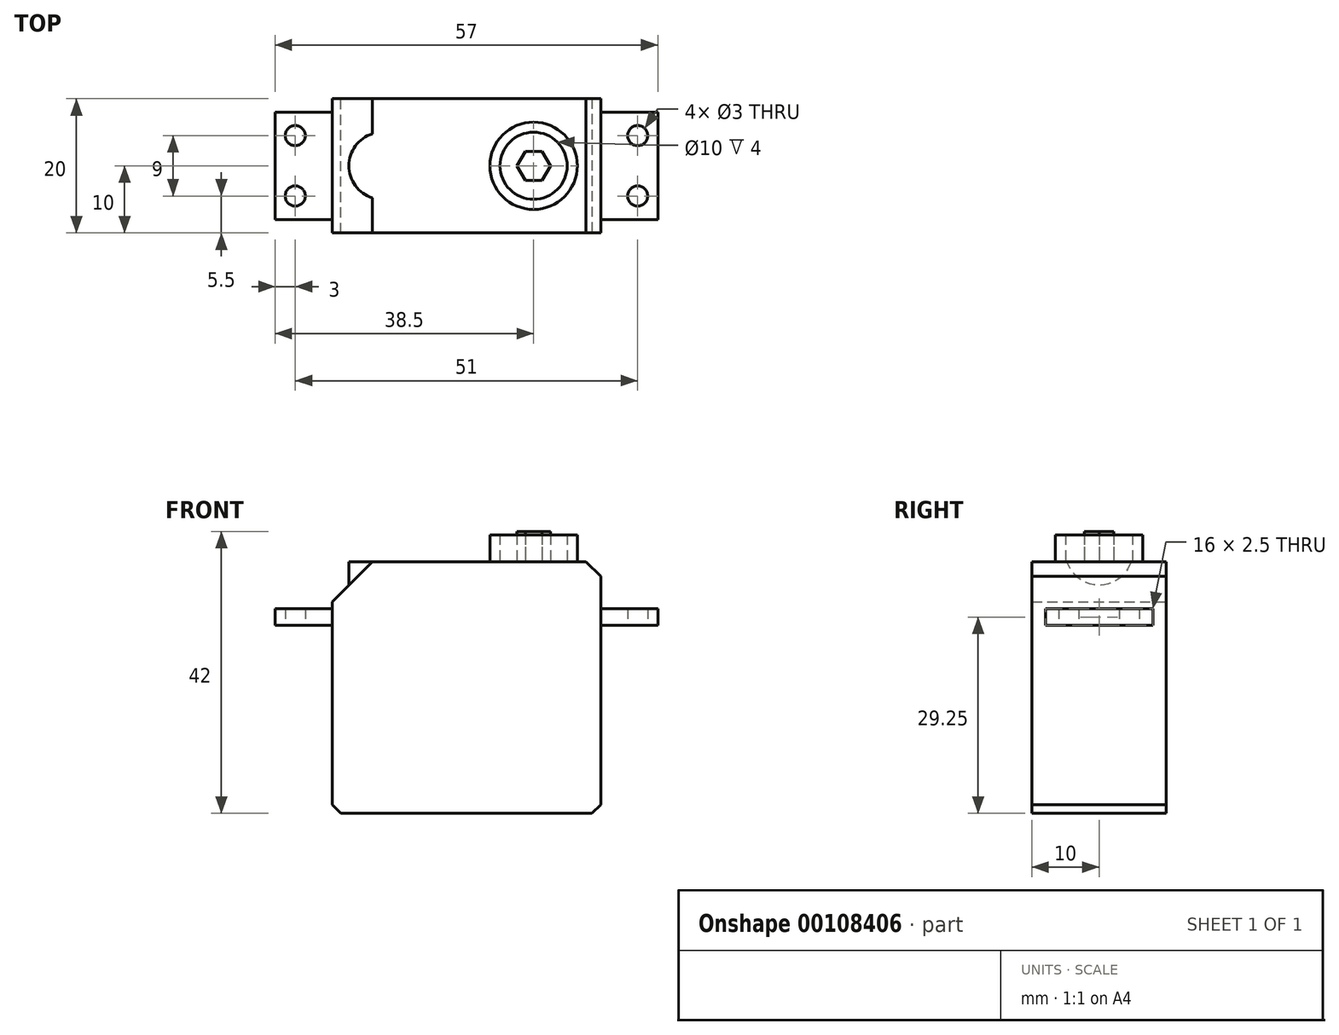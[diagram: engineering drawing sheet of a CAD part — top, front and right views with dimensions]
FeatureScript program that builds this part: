
annotation { "Feature Type Name" : "Feature", "Feature Type Description" : "" }
export const myFeature = defineFeature(function(context is Context, id is Id, definition is map)
    precondition{}
    {
        {
            var Q0;
            Q0=qCreatedBy(makeId("Top.planeOp"),FACE);
            var sketch = newSketch(context, id + "F0", { "sketchPlane" : qUnion([Q0])});
            skLineSegment(sketch, "E0.bottom", {"start": v(-20, 10) * mm, "end": v(20, 10) * mm});
            skLineSegment(sketch, "E0.top", {"start": v(-20, -10) * mm, "end": v(20, -10) * mm});
            skLineSegment(sketch, "E0.left", {"start": v(-20, 10) * mm, "end": v(-20, -10) * mm});
            skLineSegment(sketch, "E0.right", {"start": v(20, 10) * mm, "end": v(20, -10) * mm});
            skPoint(sketch, "E0.middle", {"position": v(0, 0) * mm});
            skLineSegment(sketch, "E1", {"start": v(-20, 0) * mm, "end": v(10, 0) * mm, "construction": true});
            skLineSegment(sketch, "E2", {"start": v(20, 10) * mm, "end": v(20, 8) * mm});
            skLineSegment(sketch, "E3", {"start": v(20, -10) * mm, "end": v(20, -8) * mm});
            skLineSegment(sketch, "E4", {"start": v(-20, -10) * mm, "end": v(-20, -8) * mm});
            skLineSegment(sketch, "E5", {"start": v(-20, 10) * mm, "end": v(-20, 8) * mm});
            skLineSegment(sketch, "E6", {"start": v(20, 8) * mm, "end": v(28.5, 8) * mm});
            skLineSegment(sketch, "E7", {"start": v(20, -8) * mm, "end": v(28.5, -8) * mm});
            skLineSegment(sketch, "E8", {"start": v(-20, -8) * mm, "end": v(-28.5, -8) * mm});
            skLineSegment(sketch, "E9", {"start": v(-20, 8) * mm, "end": v(-28.5, 8) * mm});
            skLineSegment(sketch, "E10", {"start": v(28.5, -8) * mm, "end": v(28.5, 8) * mm});
            skLineSegment(sketch, "E11", {"start": v(-28.5, -8) * mm, "end": v(-28.5, 8) * mm});
            skCircle(sketch, "E12.cCircle", {"center": v(10, 0) * mm, "radius": 2.17 * mm, "construction": true});
            skLineSegment(sketch, "E12.0", {"start": v(8.75, 2.17) * mm, "end": v(11.25, 2.17) * mm});
            skLineSegment(sketch, "E12.1", {"start": v(11.25, 2.17) * mm, "end": v(12.5, 0) * mm});
            skLineSegment(sketch, "E12.2", {"start": v(12.5, 0) * mm, "end": v(11.25, -2.17) * mm});
            skLineSegment(sketch, "E12.3", {"start": v(11.25, -2.17) * mm, "end": v(8.75, -2.17) * mm});
            skLineSegment(sketch, "E12.4", {"start": v(8.75, -2.17) * mm, "end": v(7.5, 0) * mm});
            skLineSegment(sketch, "E12.5", {"start": v(7.5, 0) * mm, "end": v(8.75, 2.17) * mm});
            skPoint(sketch, "E12.0.midPoint", {"position": v(10, 2.17) * mm});
            skCircle(sketch, "E13", {"center": v(10, 0) * mm, "radius": 5 * mm});
            skLineSegment(sketch, "E14", {"start": v(-20, 0) * mm, "end": v(-5.25, 0) * mm, "construction": true});
            skPoint(sketch, "E15.middle", {"position": v(-5.25, 0) * mm});
            skLineSegment(sketch, "E16", {"start": v(-28.5, 0) * mm, "end": v(-25.5, 0) * mm, "construction": true});
            skPoint(sketch, "E16.endSnap0", {"position": v(-28.5, 0) * mm});
            skLineSegment(sketch, "E17", {"start": v(-25.5, 0) * mm, "end": v(-25.5, 4.5) * mm, "construction": true});
            skLineSegment(sketch, "E18", {"start": v(-25.5, 0) * mm, "end": v(-25.5, -4.5) * mm, "construction": true});
            skCircle(sketch, "E19", {"center": v(-25.5, 4.5) * mm, "radius": 1.5 * mm});
            skCircle(sketch, "E20", {"center": v(-25.5, -4.5) * mm, "radius": 1.5 * mm});
            skLineSegment(sketch, "E21", {"start": v(28.5, 0) * mm, "end": v(25.5, 0) * mm, "construction": true});
            skPoint(sketch, "E21.endSnap0", {"position": v(28.5, 0) * mm});
            skLineSegment(sketch, "E22", {"start": v(25.5, 0) * mm, "end": v(25.5, 4.5) * mm, "construction": true});
            skLineSegment(sketch, "E23", {"start": v(25.5, 0) * mm, "end": v(25.5, -4.5) * mm, "construction": true});
            skCircle(sketch, "E24", {"center": v(25.5, 4.5) * mm, "radius": 1.5 * mm});
            skCircle(sketch, "E25", {"center": v(25.5, -4.5) * mm, "radius": 1.5 * mm});
            skCircle(sketch, "E26", {"center": v(10, 0) * mm, "radius": 6.5 * mm});
            skLineSegment(sketch, "E27", {"start": v(20, 0) * mm, "end": v(19.5, 0) * mm});
            skCircle(sketch, "E28", {"center": v(10, 0) * mm, "radius": 9.5 * mm});
            skLineSegment(sketch, "E29", {"start": v(-20, 0) * mm, "end": v(-12.5, 0) * mm});
            skCircle(sketch, "E30", {"center": v(-12.5, 0) * mm, "radius": 5 * mm});
            skLineSegment(sketch, "E31", {"start": v(10, 0) * mm, "end": v(10, -6.5) * mm});
            skLineSegment(sketch, "E32", {"start": v(10, -6.5) * mm, "end": v(10, 6.5) * mm});
            skLineSegment(sketch, "E33", {"start": v(10, 0) * mm, "end": v(10, 5) * mm});
            skLineSegment(sketch, "E34", {"start": v(10, 0) * mm, "end": v(10, -5) * mm});
            skPoint(sketch, "E34.endSnap0", {"position": v(10, -3.25) * mm});
            skSolve(sketch);
        }
        {
            var Q0;
            Q0=makeQuery(id+"F0.imprint","IMPRINT",FACE,{"disambiguationData":[TD([[makeQuery(id+"F0.imprint","IMPRINT",EDGE,{"derivedFrom":sQuery(id+"F0.wireOp",EDGE,"E12.0")}),-1.0]])]});
            extrude(context, id + "F1", {"entities" : qUnion([Q0]), "depth" : 14 * mm});
        }
        {
            var Q0;
            Q0=makeQuery(id+"F0.imprint","IMPRINT",FACE,{"disambiguationData":[TD([[makeQuery(id+"F0.imprint","IMPRINT",EDGE,{"derivedFrom":sQuery(id+"F0.wireOp",EDGE,"E13")}),-1.0]])]});
            extrude(context, id + "F2", {"entities" : qUnion([Q0]), "operationType" : NewBodyOperationType.ADD, "depth" : 13.5 * mm});
        }
        {
            var Q0;
            Q0=makeQuery(id+"F0.imprint","IMPRINT",FACE,{"disambiguationData":[TD([[makeQuery(id+"F0.imprint","IMPRINT",EDGE,{"derivedFrom":sQuery(id+"F0.wireOp",EDGE,"E26")}),-1.0]])]});
            var Q1;
            Q1=makeQuery(id+"F0.imprint","IMPRINT",FACE,{"disambiguationData":[TD([[makeQuery(id+"F0.imprint","IMPRINT",EDGE,{"derivedFrom":sQuery(id+"F0.wireOp",EDGE,"E12.0")}),1.0]])]});
            extrude(context, id + "F3", {"entities" : qUnion([Q0, Q1]), "operationType" : NewBodyOperationType.ADD, "depth" : 9.5 * mm});
        }
        {
            var Q0;
            Q0=makeQuery(id+"F0.imprint","IMPRINT",FACE,{"disambiguationData":[TD([[makeQuery(id+"F0.imprint","IMPRINT",EDGE,{"derivedFrom":sQuery(id+"F0.wireOp",EDGE,"E0.bottom")}),-1.0]])]});
            var Q1;
            Q1=makeQuery(id+"F0.imprint","IMPRINT",FACE,{"disambiguationData":[TD([[makeQuery(id+"F0.imprint","IMPRINT",EDGE,{"derivedFrom":sQuery(id+"F0.wireOp",EDGE,"E26")}),-1.0]])]});
            extrude(context, id + "F4", {"entities" : qUnion([Q0, Q1]), "operationType" : NewBodyOperationType.ADD, "depth" : 9.5 * mm});
        }
        {
            var Q0;
            Q0=makeQuery(id+"F0.imprint","IMPRINT",FACE,{"disambiguationData":[TD([[makeQuery(id+"F0.imprint","IMPRINT",EDGE,{"derivedFrom":sQuery(id+"F0.wireOp",EDGE,"E0.bottom")}),-1.0]])]});
            var Q1;
            Q1=makeQuery(id+"F0.imprint","IMPRINT",FACE,{"disambiguationData":[TD([[makeQuery(id+"F0.imprint","IMPRINT",EDGE,{"derivedFrom":sQuery(id+"F0.wireOp",EDGE,"E26")}),-1.0]])]});
            var Q2;
            Q2=makeQuery(id+"F0.imprint","IMPRINT",FACE,{"disambiguationData":[TD([[makeQuery(id+"F0.imprint","IMPRINT",EDGE,{"derivedFrom":sQuery(id+"F0.wireOp",EDGE,"E12.0")}),-1.0]])]});
            var Q3;
            Q3=makeQuery(id+"F0.imprint","IMPRINT",FACE,{"disambiguationData":[TD([[makeQuery(id+"F0.imprint","IMPRINT",EDGE,{"derivedFrom":sQuery(id+"F0.wireOp",EDGE,"E12.0")}),1.0]])]});
            var Q4;
            Q4=makeQuery(id+"F0.imprint","IMPRINT",FACE,{"disambiguationData":[TD([[makeQuery(id+"F0.imprint","IMPRINT",EDGE,{"derivedFrom":sQuery(id+"F0.wireOp",EDGE,"E13")}),-1.0]])]});
            var Q5;
            Q5=makeQuery(id+"F0.imprint","IMPRINT",FACE,{"disambiguationData":[TD([[makeQuery(id+"F0.imprint","IMPRINT",EDGE,{"derivedFrom":sQuery(id+"F0.wireOp",EDGE,"E30")}),1.0]])]});
            extrude(context, id + "F5", {"entities" : qUnion([Q0, Q1, Q2, Q3, Q4, Q5]), "operationType" : NewBodyOperationType.ADD, "oppositeDirection" : true, "depth" : 28 * mm});
        }
        {
            var Q0;
            {var subQ1=sQuery(id+"F0.wireOp",EDGE,"E6");Q0=makeQuery(id+"F0.imprint","IMPRINT",FACE,{"disambiguationData":[TD([[makeQuery(id+"F0.imprint","IMPRINT",EDGE,{"derivedFrom":subQ1}),-1.0]])]});}
            var Q1;
            Q1=makeQuery(id+"F0.imprint","IMPRINT",FACE,{"disambiguationData":[TD([[makeQuery(id+"F0.imprint","IMPRINT",EDGE,{"derivedFrom":sQuery(id+"F0.wireOp",EDGE,"E0.left")}),-1.0]])]});
            extrude(context, id + "F6", {"entities" : qUnion([Q0, Q1]), "operationType" : NewBodyOperationType.ADD, "depth" : 2.5 * mm});
        }
        {
            var Q0;
            Q0=makeQuery(id+"F4.opExtrude","CAP_EDGE",EDGE,{"disambiguationData":[OSD([sQuery(id+"F0.wireOp",EDGE,"E0.right"),sQuery(id+"F0.wireOp",EDGE,"E2"),sQuery(id+"F0.wireOp",EDGE,"E3")])],"isStart":false});
            chamfer(context, id + "F7", {"entities" : qUnion([Q0]), "width" : 2.2 * mm});
        }
        {
            var Q0;
            Q0=makeQuery(id+"F4.opExtrude","CAP_EDGE",EDGE,{"disambiguationData":[OSD([sQuery(id+"F0.wireOp",EDGE,"E0.left"),sQuery(id+"F0.wireOp",EDGE,"E4"),sQuery(id+"F0.wireOp",EDGE,"E5")])],"isStart":false});
            chamfer(context, id + "F8", {"entities" : qUnion([Q0]), "width" : 6 * mm, "tangentPropagation" : true});
        }
        {
            var Q0;
            Q0=makeQuery(id+"F0.imprint","IMPRINT",FACE,{"disambiguationData":[TD([[makeQuery(id+"F0.imprint","IMPRINT",EDGE,{"derivedFrom":sQuery(id+"F0.wireOp",EDGE,"E30")}),1.0]])]});
            extrude(context, id + "F9", {"entities" : qUnion([Q0]), "operationType" : NewBodyOperationType.ADD, "depth" : 9.5 * mm});
        }
        {
            var Q0;
            Q0=makeQuery(id+"F5.opExtrude","CAP_EDGE",EDGE,{"disambiguationData":[OSD([sQuery(id+"F0.wireOp",EDGE,"E0.right"),sQuery(id+"F0.wireOp",EDGE,"E2"),sQuery(id+"F0.wireOp",EDGE,"E3")])],"isStart":false});
            var Q1;
            Q1=makeQuery(id+"F5.opExtrude","CAP_EDGE",EDGE,{"disambiguationData":[OSD([sQuery(id+"F0.wireOp",EDGE,"E0.left"),sQuery(id+"F0.wireOp",EDGE,"E4"),sQuery(id+"F0.wireOp",EDGE,"E5")])],"isStart":false});
            chamfer(context, id + "F10", {"entities" : qUnion([Q0, Q1]), "width" : 1.3 * mm, "tangentPropagation" : true});
        }
    });
